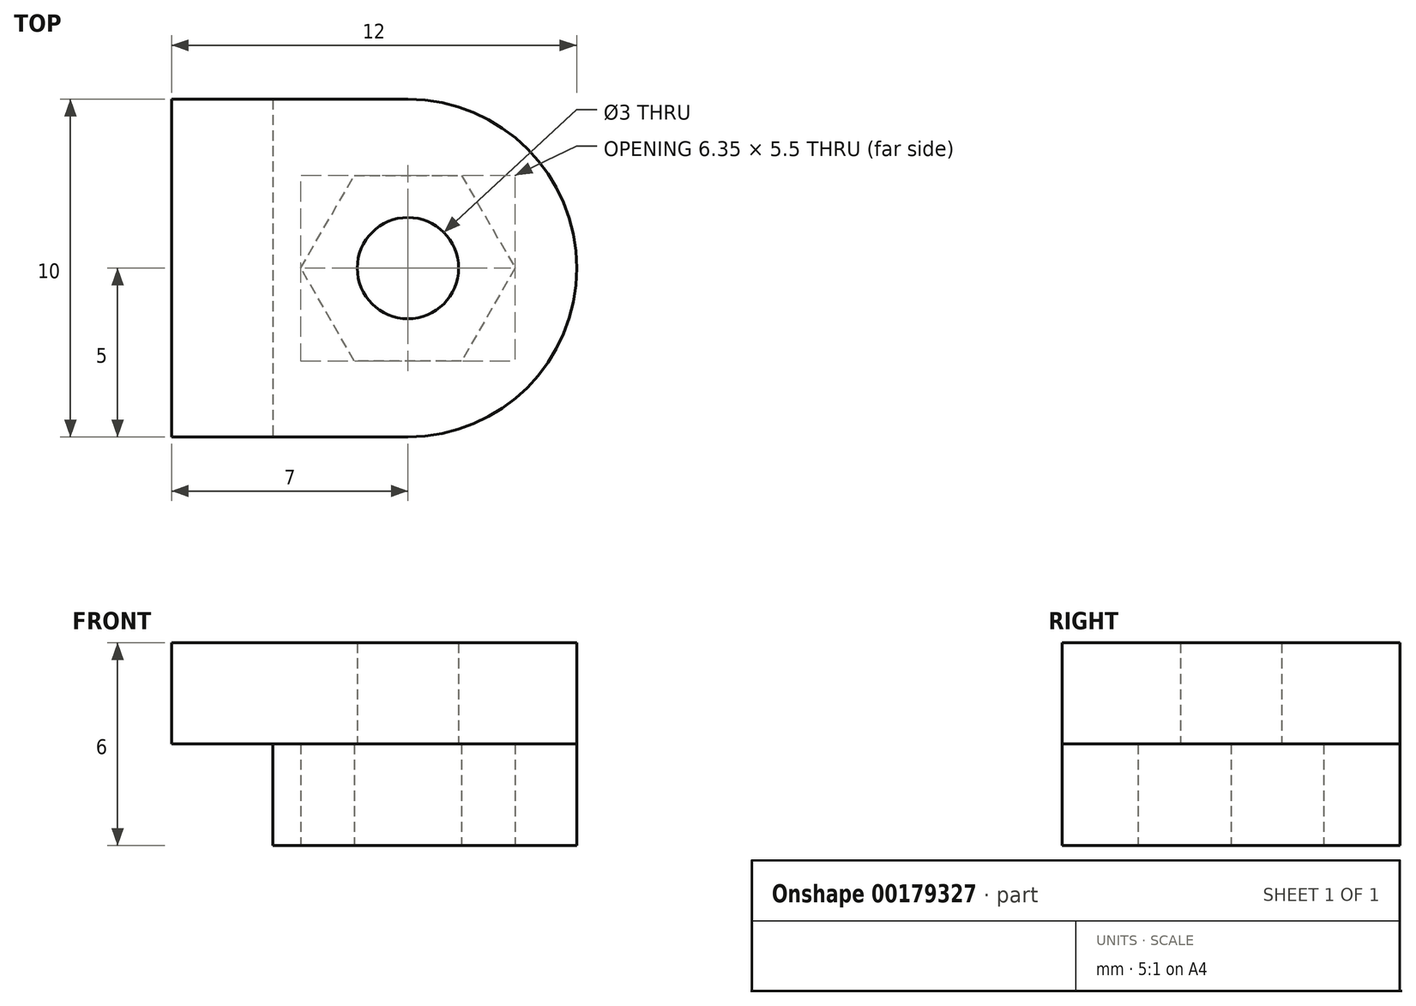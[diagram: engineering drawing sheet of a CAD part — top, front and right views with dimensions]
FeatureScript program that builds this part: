
annotation { "Feature Type Name" : "Feature", "Feature Type Description" : "" }
export const myFeature = defineFeature(function(context is Context, id is Id, definition is map)
    precondition{}
    {
        {
            assignVariable(context, id + "F0", {"name" : "thickness", "anyValue" : 3 * mm});
        }
        {
            var Q0;
            Q0=qCreatedBy(makeId("Top.planeOp"),FACE);
            var sketch = newSketch(context, id + "F1", { "sketchPlane" : qUnion([Q0])});
            skCircle(sketch, "E0.cCircle", {"center": v(0, 0) * mm, "radius": 3.18 * mm, "construction": true});
            skLineSegment(sketch, "E0.0", {"start": v(3.18, 0) * mm, "end": v(1.59, -2.75) * mm});
            skLineSegment(sketch, "E0.1", {"start": v(1.59, -2.75) * mm, "end": v(-1.59, -2.75) * mm});
            skLineSegment(sketch, "E0.2", {"start": v(-1.59, -2.75) * mm, "end": v(-3.18, 0) * mm});
            skLineSegment(sketch, "E0.3", {"start": v(-3.18, 0) * mm, "end": v(-1.59, 2.75) * mm});
            skLineSegment(sketch, "E0.4", {"start": v(-1.59, 2.75) * mm, "end": v(1.59, 2.75) * mm});
            skLineSegment(sketch, "E0.5", {"start": v(1.59, 2.75) * mm, "end": v(3.18, 0) * mm});
            skArc(sketch, "E1", {"start": v(0, 5) * mm, "mid": v(5, 0) * mm, "end": v(0, -5) * mm});
            skLineSegment(sketch, "E2", {"start": v(0, 5) * mm, "end": v(-4, 5) * mm});
            skLineSegment(sketch, "E3", {"start": v(-4, 5) * mm, "end": v(-4, -5) * mm});
            skLineSegment(sketch, "E4", {"start": v(-4, -5) * mm, "end": v(0, -5) * mm});
            skSolve(sketch);
        }
        {
            var Q0;
            Q0 = qSketchRegion(id + "F1", true);
            extrude(context, id + "F2", {"entities" : qUnion([Q0]), "depth" : getVariable(context, 'thickness')});
        }
        {
            var Q0;
            Q0=makeQuery(id+"F2.opExtrude","CAP_FACE",FACE,{"disambiguationData":[OSD([sQuery(id+"F1.wireOp",EDGE,"E0.0"),sQuery(id+"F1.wireOp",EDGE,"E0.1"),sQuery(id+"F1.wireOp",EDGE,"E0.2"),sQuery(id+"F1.wireOp",EDGE,"E0.3"),sQuery(id+"F1.wireOp",EDGE,"E0.4"),sQuery(id+"F1.wireOp",EDGE,"E0.5"),sQuery(id+"F1.wireOp",EDGE,"E1"),sQuery(id+"F1.wireOp",EDGE,"E2"),sQuery(id+"F1.wireOp",EDGE,"E3"),sQuery(id+"F1.wireOp",EDGE,"E4")])],"isStart":false});
            var sketch = newSketch(context, id + "F3", { "sketchPlane" : qUnion([Q0])});
            skCircle(sketch, "E5", {"center": v(0, 0) * mm, "radius": 1.5 * mm});
            skLineSegment(sketch, "E6.0", {"start": v(0, 5) * mm, "end": v(-4, 5) * mm});
            skArc(sketch, "E6.1", {"start": v(0, 5) * mm, "mid": v(5, 0) * mm, "end": v(0, -5) * mm});
            skLineSegment(sketch, "E6.2", {"start": v(-4, -5) * mm, "end": v(0, -5) * mm});
            skLineSegment(sketch, "E7", {"start": v(-4, 5) * mm, "end": v(-7, 5) * mm});
            skLineSegment(sketch, "E8", {"start": v(-7, 5) * mm, "end": v(-7, -5) * mm});
            skLineSegment(sketch, "E9", {"start": v(-7, -5) * mm, "end": v(-4, -5) * mm});
            skSolve(sketch);
        }
        {
            var Q0;
            Q0 = qSketchRegion(id + "F3", true);
            extrude(context, id + "F4", {"entities" : qUnion([Q0]), "depth" : getVariable(context, 'thickness')});
        }
    });
